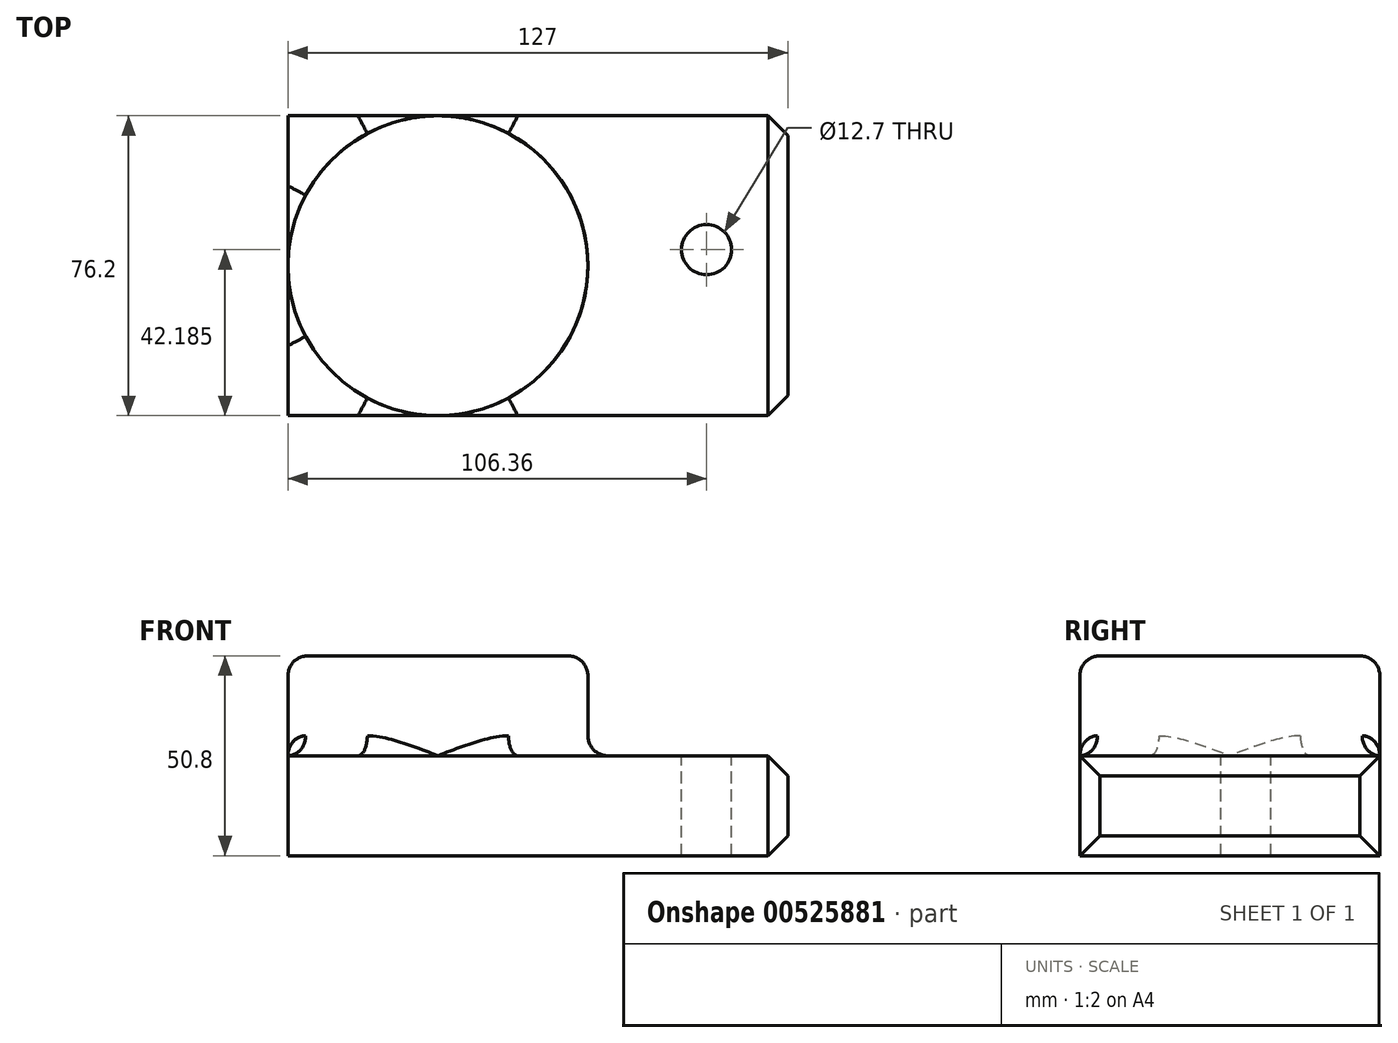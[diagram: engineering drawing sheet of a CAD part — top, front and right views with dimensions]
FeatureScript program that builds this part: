
annotation { "Feature Type Name" : "Feature", "Feature Type Description" : "" }
export const myFeature = defineFeature(function(context is Context, id is Id, definition is map)
    precondition{}
    {
        {
            var Q0;
            Q0=qCreatedBy(makeId("Top.planeOp"),FACE);
            var sketch = newSketch(context, id + "F0", { "sketchPlane" : qUnion([Q0])});
            skLineSegment(sketch, "E0.bottom", {"start": v(0, 0) * mm, "end": v(127, 0) * mm});
            skLineSegment(sketch, "E0.top", {"start": v(0, 76.2) * mm, "end": v(127, 76.2) * mm});
            skLineSegment(sketch, "E0.left", {"start": v(0, 0) * mm, "end": v(0, 76.2) * mm});
            skLineSegment(sketch, "E0.right", {"start": v(127, 0) * mm, "end": v(127, 76.2) * mm});
            skPoint(sketch, "E1.middle", {"position": v(0, 0) * mm});
            skCircle(sketch, "E2", {"center": v(38.1, 38.1) * mm, "radius": 38.1 * mm});
            skPoint(sketch, "E2.first.point", {"position": v(38.1, 76.2) * mm});
            skPoint(sketch, "E2.second.point", {"position": v(0, 38.1) * mm});
            skPoint(sketch, "E2.third.point", {"position": v(38.1, 0) * mm});
            skPoint(sketch, "E3", {"position": v(106.36, 42.18) * mm});
            skSolve(sketch);
        }
        {
            var Q0;
            {var subQ0=sQuery(id+"F0.wireOp",EDGE,"E2");var subQ1=makeQuery(id+"F0.imprint","INTERSECT",VERTEX,{"derivedFrom":[sQuery(id+"F0.wireOp",EDGE,"E0.top"),subQ0]});Q0=makeQuery(id+"F0.imprint","IMPRINT",FACE,{"disambiguationData":[TD([[makeQuery(id+"F0.imprint","IMPRINT",EDGE,{"disambiguationData":[TD([[subQ1,-1.0]])],"derivedFrom":subQ0}),1.0]])]});}
            extrude(context, id + "F1", {"entities" : qUnion([Q0]), "depth" : 25.4 * mm, "offsetDistance" : 25.4 * mm});
        }
        {
            var Q0;
            Q0 = qSketchRegion(id + "F0", true);
            extrude(context, id + "F2", {"entities" : qUnion([Q0]), "operationType" : NewBodyOperationType.ADD, "oppositeDirection" : true, "depth" : 25.4 * mm, "offsetDistance" : 25.4 * mm});
        }
        {
            var Q0;
            Q0=makeQuery(id+"F1.opExtrude","CAP_EDGE",EDGE,{"disambiguationData":[OSD([sQuery(id+"F0.wireOp",EDGE,"E2")])],"isStart":false});
            var Q1;
            {var subQ0=sQuery(id+"F0.wireOp",EDGE,"E2");var subQ1=sQuery(id+"F0.wireOp",EDGE,"E0.bottom");var subQ2=sQuery(id+"F0.wireOp",EDGE,"E0.top");Q1=makeQuery(id+"F2.boolean.opBoolean","SPLIT",EDGE,{"disambiguationData":[TD([makeQuery(id+"F1.opExtrude","SWEPT_FACE",FACE,{"disambiguationData":[OSD([subQ0])]}),makeQuery(id+"F2.opExtrude","SWEPT_FACE",FACE,{"disambiguationData":[OSD([subQ1])]}),makeQuery(id+"F2.opExtrude","CAP_FACE",FACE,{"disambiguationData":[OSD([subQ1,subQ2,sQuery(id+"F0.wireOp",EDGE,"E0.left"),sQuery(id+"F0.wireOp",EDGE,"E0.right")])],"isStart":true}),makeQuery(id+"F2.opExtrude","SWEPT_FACE",FACE,{"disambiguationData":[OSD([subQ2])]})])],"derivedFrom":makeQuery(id+"F1.opExtrude","CAP_EDGE",EDGE,{"disambiguationData":[OSD([subQ0])],"isStart":true})});}
            fillet(context, id + "F3", {"entities" : qUnion([Q0, Q1]), "radius" : 5.08 * mm, "tangentPropagation" : true, "allowEdgeOverflow" : false});
        }
        {
            var Q0;
            Q0=makeQuery(id+"F2.opExtrude","CAP_EDGE",EDGE,{"disambiguationData":[OSD([sQuery(id+"F0.wireOp",EDGE,"E0.right")])],"isStart":true});
            var Q1;
            Q1=makeQuery(id+"F2.opExtrude","CAP_EDGE",EDGE,{"disambiguationData":[OSD([sQuery(id+"F0.wireOp",EDGE,"E0.right")])],"isStart":false});
            var Q2;
            Q2=makeQuery(id+"F2.opExtrude","SWEPT_EDGE",EDGE,{"disambiguationData":[OSD([sQuery(id+"F0.wireOp",EDGE,"E0.top"),sQuery(id+"F0.wireOp",EDGE,"E0.right")])]});
            var Q3;
            Q3=makeQuery(id+"F2.opExtrude","SWEPT_EDGE",EDGE,{"disambiguationData":[OSD([sQuery(id+"F0.wireOp",EDGE,"E0.bottom"),sQuery(id+"F0.wireOp",EDGE,"E0.right")])]});
            chamfer(context, id + "F4", {"entities" : qUnion([Q0, Q1, Q2, Q3]), "width" : 5.08 * mm, "tangentPropagation" : true});
        }
        {
            var Q0;
            {var subQ0=sQuery(id+"F0.wireOp",EDGE,"E0.top");var subQ1=sQuery(id+"F0.wireOp",EDGE,"E0.right");var subQ2=sQuery(id+"F0.wireOp",EDGE,"E0.bottom");var subQ3=makeQuery(id+"F2.opExtrude","CAP_FACE",FACE,{"disambiguationData":[OSD([subQ2,subQ0,sQuery(id+"F0.wireOp",EDGE,"E0.left"),subQ1])],"isStart":true});Q0=makeQuery(id+"F2.boolean.opBoolean","SPLIT",FACE,{"disambiguationData":[TD([makeQuery(id+"F1.opExtrude","SWEPT_FACE",FACE,{"disambiguationData":[OSD([sQuery(id+"F0.wireOp",EDGE,"E2")])]}),makeQuery(id+"F2.opExtrude","SWEPT_FACE",FACE,{"disambiguationData":[OSD([subQ2])]}),subQ3,makeQuery(id+"F2.opExtrude","SWEPT_FACE",FACE,{"disambiguationData":[OSD([subQ0])]}),makeQuery(id+"F2.opExtrude","SWEPT_FACE",FACE,{"disambiguationData":[OSD([subQ1])]})])],"derivedFrom":subQ3});}
            var sketch = newSketch(context, id + "F5", { "sketchPlane" : qUnion([Q0])});
            skPoint(sketch, "E4", {"position": v(106.36, 42.18) * mm});
            skSolve(sketch);
        }
        {
            var Q0;
            Q0=sQuery(id+"F5.wireOp",VERTEX,"E4");
            var Q1;
            Q1=makeQuery(id+"F1.opExtrude","SWEPT_BODY",BODY,{"disambiguationData":[OSD([sQuery(id+"F0.wireOp",EDGE,"E2")])]});
            hole(context, id + "F6", {"style" : HoleStyle.C_BORE, "endStyle" : HoleEndStyle.THROUGH, "holeDiameter" : 12.7 * mm, "cBoreDiameter" : 12.7 * mm, "cBoreDepth" : 0.25 * mm, "isTappedThrough" : true, "tappedDepth" : 12.7 * mm, "tapClearance" : 3, "locations" : qUnion([Q0]), "scope" : qUnion([Q1])});
        }
    });
